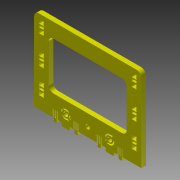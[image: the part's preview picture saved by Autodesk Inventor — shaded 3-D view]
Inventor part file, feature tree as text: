
AUTODESK INVENTOR PART (.ipt)
format: ipt  version: 2012 (Build 160160000, 160)  size: 529,920 bytes
history: native  units: in
note: dims shown in document units (in); Inventor stores cm internally (conversion verified against a paired STEP export)
features: other x4, extrude x2
ambient origin geometry x8: Origin, YZ Plane, XZ Plane, XY Plane, X Axis, Y Axis, Z Axis, Center Point
bodies: Solid1 (feature_tree)
feature tree (6):
  other  "skeleton.ipt"
  other  "POCKET_1-16"
  other  "STOCK_12MM"
  extrude  "Extrusion1"  Depth=0.3937in
  extrude  "Extrusion2"  Depth=0.4724in
  other  "THROUGH-CUT"
